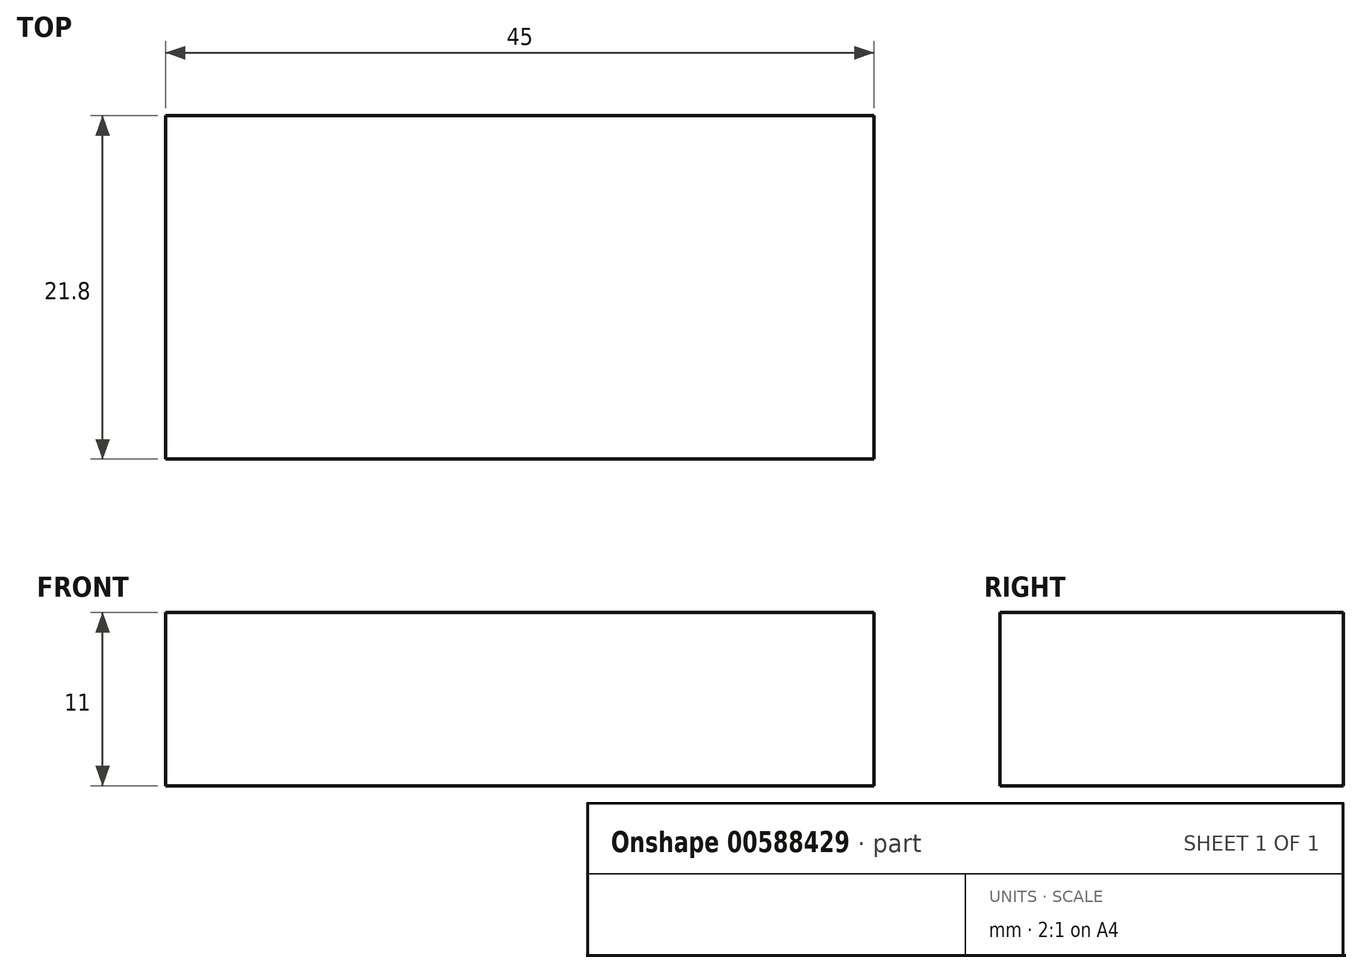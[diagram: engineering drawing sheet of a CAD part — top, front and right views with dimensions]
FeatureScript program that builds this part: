
annotation { "Feature Type Name" : "Feature", "Feature Type Description" : "" }
export const myFeature = defineFeature(function(context is Context, id is Id, definition is map)
    precondition{}
    {
        {
            var Q0;
            Q0=qCreatedBy(makeId("Top.planeOp"),FACE);
            var sketch = newSketch(context, id + "F0", { "sketchPlane" : qUnion([Q0])});
            skLineSegment(sketch, "E0.bottom", {"start": v(-21.16, 16.92) * mm, "end": v(23.84, 16.92) * mm});
            skLineSegment(sketch, "E0.top", {"start": v(-21.16, -4.88) * mm, "end": v(23.84, -4.88) * mm});
            skLineSegment(sketch, "E0.left", {"start": v(-21.16, 16.92) * mm, "end": v(-21.16, -4.88) * mm});
            skLineSegment(sketch, "E0.right", {"start": v(23.84, 16.92) * mm, "end": v(23.84, -4.88) * mm});
            skSolve(sketch);
        }
        {
            var Q0;
            Q0 = qSketchRegion(id + "F0", true);
            extrude(context, id + "F1", {"entities" : qUnion([Q0]), "depth" : 11 * mm, "offsetDistance" : 25 * mm});
        }
    });
